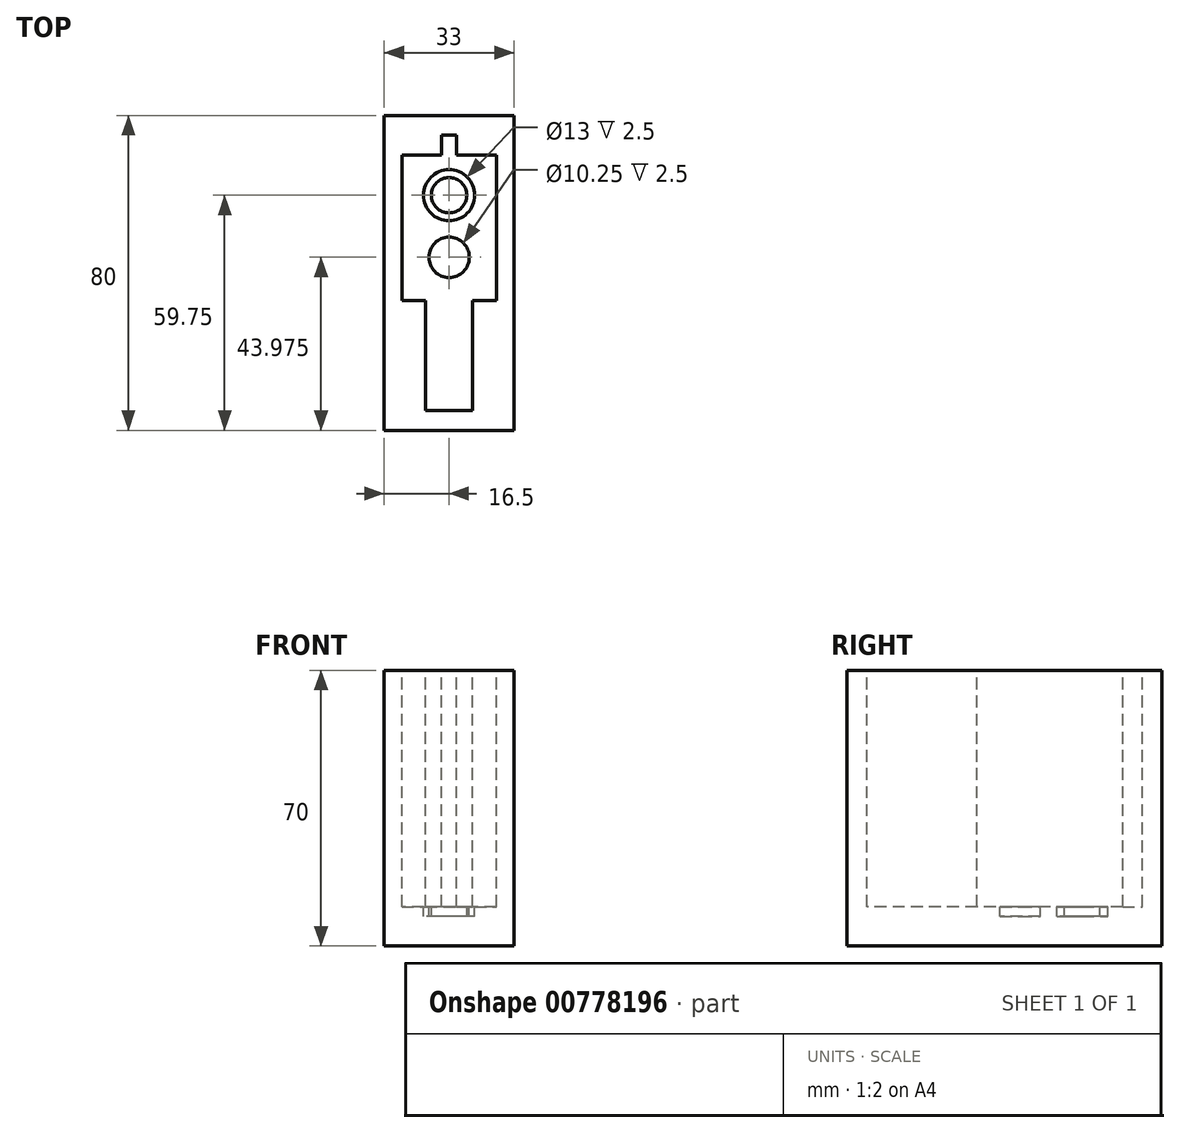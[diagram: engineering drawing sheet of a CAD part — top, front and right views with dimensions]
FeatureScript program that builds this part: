
annotation { "Feature Type Name" : "Feature", "Feature Type Description" : "" }
export const myFeature = defineFeature(function(context is Context, id is Id, definition is map)
    precondition{}
    {
        {
            var Q0;
            Q0=qCreatedBy(makeId("Top.planeOp"),FACE);
            var sketch = newSketch(context, id + "F0", { "sketchPlane" : qUnion([Q0])});
            skLineSegment(sketch, "E0", {"start": v(-87.5, 0) * mm, "end": v(87.5, 0) * mm, "construction": true});
            skLineSegment(sketch, "E1", {"start": v(-87.5, 0) * mm, "end": v(-87.5, 25) * mm, "construction": true});
            skLineSegment(sketch, "E2", {"start": v(-87.5, 25) * mm, "end": v(87.5, 25) * mm, "construction": true});
            skLineSegment(sketch, "E3", {"start": v(87.5, 25) * mm, "end": v(87.5, 0) * mm, "construction": true});
            skLineSegment(sketch, "E4.bottom", {"start": v(-87.5, 25) * mm, "end": v(-54.5, 25) * mm});
            skLineSegment(sketch, "E4.top", {"start": v(-87.5, -55) * mm, "end": v(-54.5, -55) * mm});
            skLineSegment(sketch, "E4.left", {"start": v(-87.5, 25) * mm, "end": v(-87.5, -55) * mm});
            skLineSegment(sketch, "E4.right", {"start": v(-54.5, 25) * mm, "end": v(-54.5, -55) * mm});
            skSolve(sketch);
        }
        {
            var Q0;
            Q0 = qSketchRegion(id + "F0", true);
            extrude(context, id + "F1", {"entities" : qUnion([Q0]), "depth" : 70 * mm, "offsetDistance" : 25 * mm});
        }
        {
            var Q0;
            Q0=makeQuery(id+"F1.opExtrude","CAP_FACE",FACE,{"disambiguationData":[OSD([sQuery(id+"F0.wireOp",EDGE,"E4.bottom"),sQuery(id+"F0.wireOp",EDGE,"E4.top"),sQuery(id+"F0.wireOp",EDGE,"E4.left"),sQuery(id+"F0.wireOp",EDGE,"E4.right")])],"isStart":false});
            var sketch = newSketch(context, id + "F2", { "sketchPlane" : qUnion([Q0])});
            skLineSegment(sketch, "E5", {"start": v(-71, 25) * mm, "end": v(-71, -55) * mm, "construction": true});
            skLineSegment(sketch, "E6", {"start": v(-87.5, -15) * mm, "end": v(-54.5, -15) * mm, "construction": true});
            skLineSegment(sketch, "E7", {"start": v(-72.88, 15) * mm, "end": v(-83, 15) * mm});
            skLineSegment(sketch, "E8", {"start": v(-83, 15) * mm, "end": v(-83, -22) * mm});
            skLineSegment(sketch, "E9", {"start": v(-83, -22) * mm, "end": v(-77, -22) * mm});
            skLineSegment(sketch, "E10", {"start": v(-77, -22) * mm, "end": v(-77, -50) * mm});
            skLineSegment(sketch, "E11", {"start": v(-77, -50) * mm, "end": v(-71, -50) * mm});
            skLineSegment(sketch, "E12", {"start": v(-72.88, 15) * mm, "end": v(-72.88, 20) * mm});
            skLineSegment(sketch, "E13", {"start": v(-72.88, 20) * mm, "end": v(-71, 20) * mm});
            skLineSegment(sketch, "E14.MirrorCS", {"start": v(-69.12, 20) * mm, "end": v(-71, 20) * mm});
            skLineSegment(sketch, "E15.MirrorCS", {"start": v(-65, -22) * mm, "end": v(-65, -50) * mm});
            skLineSegment(sketch, "E16.MirrorCS", {"start": v(-69.12, 15) * mm, "end": v(-69.12, 20) * mm});
            skLineSegment(sketch, "E17.MirrorCS", {"start": v(-59, -22) * mm, "end": v(-65, -22) * mm});
            skLineSegment(sketch, "E18.MirrorCS", {"start": v(-65, -50) * mm, "end": v(-71, -50) * mm});
            skLineSegment(sketch, "E19.MirrorCS", {"start": v(-69.12, 15) * mm, "end": v(-59, 15) * mm});
            skLineSegment(sketch, "E20.MirrorCS", {"start": v(-59, 15) * mm, "end": v(-59, -22) * mm});
            skSolve(sketch);
        }
        {
            var Q0;
            Q0 = qSketchRegion(id + "F2", true);
            extrude(context, id + "F3", {"entities" : qUnion([Q0]), "operationType" : NewBodyOperationType.REMOVE, "oppositeDirection" : true, "depth" : 60 * mm, "offsetDistance" : 25 * mm});
        }
        {
            var Q0;
            Q0=makeQuery(id+"F3.boolean.opBoolean","COPY",FACE,{"derivedFrom":makeQuery(id+"F3.opExtrude","CAP_FACE",FACE,{"disambiguationData":[OSD([sQuery(id+"F2.wireOp",EDGE,"E7"),sQuery(id+"F2.wireOp",EDGE,"E8"),sQuery(id+"F2.wireOp",EDGE,"E9"),sQuery(id+"F2.wireOp",EDGE,"E10"),sQuery(id+"F2.wireOp",EDGE,"E11"),sQuery(id+"F2.wireOp",EDGE,"E12"),sQuery(id+"F2.wireOp",EDGE,"E13"),sQuery(id+"F2.wireOp",EDGE,"E14.MirrorCS"),sQuery(id+"F2.wireOp",EDGE,"E15.MirrorCS"),sQuery(id+"F2.wireOp",EDGE,"E16.MirrorCS"),sQuery(id+"F2.wireOp",EDGE,"E17.MirrorCS"),sQuery(id+"F2.wireOp",EDGE,"E18.MirrorCS"),sQuery(id+"F2.wireOp",EDGE,"E19.MirrorCS"),sQuery(id+"F2.wireOp",EDGE,"E20.MirrorCS")])],"isStart":false})});
            var sketch = newSketch(context, id + "F4", { "sketchPlane" : qUnion([Q0])});
            skLineSegment(sketch, "E21", {"start": v(-71, 20) * mm, "end": v(-71, -50) * mm, "construction": true});
            skCircle(sketch, "E22", {"center": v(-71, 4.75) * mm, "radius": 4.5 * mm});
            skCircle(sketch, "E23", {"center": v(-71, 4.75) * mm, "radius": 6.5 * mm});
            skCircle(sketch, "E24", {"center": v(-71, -11.03) * mm, "radius": 5.12 * mm});
            skSolve(sketch);
        }
        {
            var Q0;
            Q0 = qSketchRegion(id + "F4", true);
            extrude(context, id + "F5", {"entities" : qUnion([Q0]), "operationType" : NewBodyOperationType.REMOVE, "oppositeDirection" : true, "depth" : 2.5 * mm, "offsetDistance" : 25 * mm});
        }
    });
